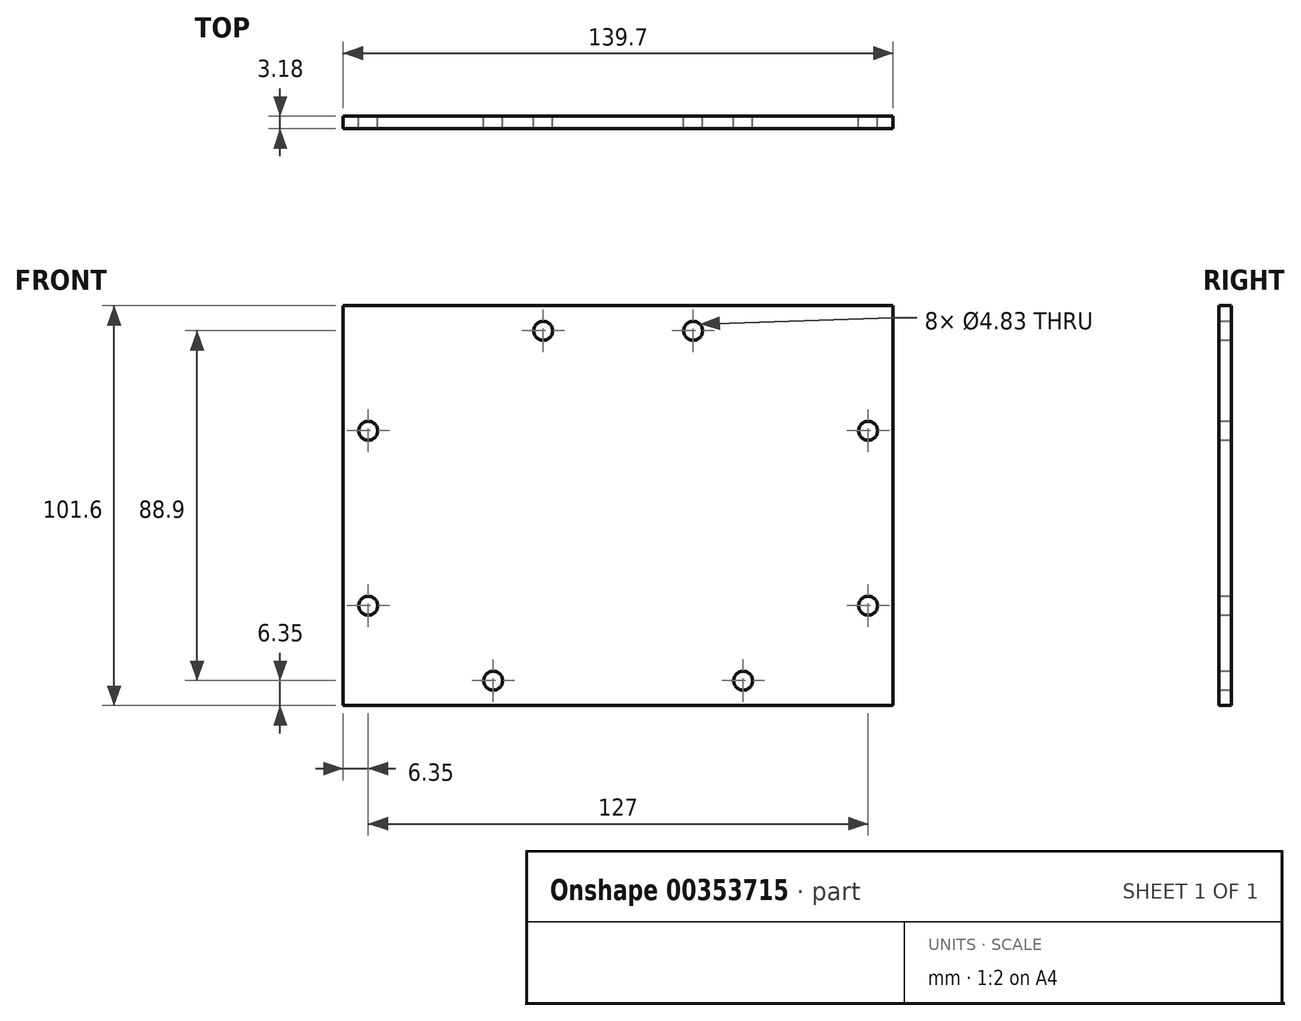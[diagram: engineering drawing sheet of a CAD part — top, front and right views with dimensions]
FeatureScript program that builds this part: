
annotation { "Feature Type Name" : "Feature", "Feature Type Description" : "" }
export const myFeature = defineFeature(function(context is Context, id is Id, definition is map)
    precondition{}
    {
        {
            var Q0;
            Q0=qCreatedBy(makeId("Front.planeOp"),FACE);
            var sketch = newSketch(context, id + "F0", { "sketchPlane" : qUnion([Q0])});
            skLineSegment(sketch, "E0.bottom", {"start": v(-69.85, 50.8) * mm, "end": v(69.85, 50.8) * mm});
            skLineSegment(sketch, "E0.top", {"start": v(-69.85, -50.8) * mm, "end": v(69.85, -50.8) * mm});
            skLineSegment(sketch, "E0.left", {"start": v(-69.85, 50.8) * mm, "end": v(-69.85, -50.8) * mm});
            skLineSegment(sketch, "E0.right", {"start": v(69.85, 50.8) * mm, "end": v(69.85, -50.8) * mm});
            skPoint(sketch, "E0.middle", {"position": v(0, 0) * mm});
            skSolve(sketch);
        }
        {
            var Q0;
            Q0 = qSketchRegion(id + "F0", true);
            extrude(context, id + "F1", {"entities" : qUnion([Q0]), "depth" : 3.17 * mm, "symmetric" : true});
        }
        {
            var Q0;
            Q0=makeQuery(id+"F1.opExtrude","CAP_FACE",FACE,{"disambiguationData":[OSD([sQuery(id+"F0.wireOp",EDGE,"E0.bottom"),sQuery(id+"F0.wireOp",EDGE,"E0.top"),sQuery(id+"F0.wireOp",EDGE,"E0.left"),sQuery(id+"F0.wireOp",EDGE,"E0.right")])],"isStart":false});
            var sketch = newSketch(context, id + "F2", { "sketchPlane" : qUnion([Q0])});
            skLineSegment(sketch, "E1", {"start": v(-69.85, 50.8) * mm, "end": v(-69.85, 0) * mm, "construction": true});
            skLineSegment(sketch, "E2", {"start": v(-69.85, 0) * mm, "end": v(-69.85, -25.4) * mm, "construction": true});
            skLineSegment(sketch, "E3", {"start": v(-69.85, 50.8) * mm, "end": v(-63.5, 50.8) * mm, "construction": true});
            skLineSegment(sketch, "E4", {"start": v(-63.5, 50.8) * mm, "end": v(-63.5, -50.8) * mm, "construction": true});
            skLineSegment(sketch, "E5", {"start": v(-69.85, 50.8) * mm, "end": v(-69.85, 19.05) * mm, "construction": true});
            skLineSegment(sketch, "E6", {"start": v(-69.85, 19.05) * mm, "end": v(69.85, 19.05) * mm, "construction": true});
            skPoint(sketch, "E7", {"position": v(-63.5, 19.05) * mm});
            skCircle(sketch, "E8", {"center": v(-63.5, 19.05) * mm, "radius": 2.41 * mm});
            skLineSegment(sketch, "E9", {"start": v(-69.85, -25.4) * mm, "end": v(69.85, -25.4) * mm, "construction": true});
            skPoint(sketch, "E10", {"position": v(-63.5, -25.4) * mm});
            skCircle(sketch, "E11", {"center": v(-63.5, -25.4) * mm, "radius": 2.41 * mm});
            skLineSegment(sketch, "E12", {"start": v(69.85, 50.8) * mm, "end": v(69.85, 44.45) * mm, "construction": true});
            skLineSegment(sketch, "E13", {"start": v(69.85, 44.45) * mm, "end": v(-69.85, 44.45) * mm, "construction": true});
            skLineSegment(sketch, "E14", {"start": v(69.85, 50.8) * mm, "end": v(63.5, 50.8) * mm, "construction": true});
            skLineSegment(sketch, "E15", {"start": v(63.5, 50.8) * mm, "end": v(63.5, -50.8) * mm, "construction": true});
            skLineSegment(sketch, "E16", {"start": v(69.85, -50.8) * mm, "end": v(69.85, -44.45) * mm, "construction": true});
            skLineSegment(sketch, "E17", {"start": v(69.85, -44.45) * mm, "end": v(-69.85, -44.45) * mm, "construction": true});
            skLineSegment(sketch, "E18", {"start": v(69.85, -50.8) * mm, "end": v(31.75, -50.8) * mm, "construction": true});
            skLineSegment(sketch, "E19", {"start": v(-69.85, -50.8) * mm, "end": v(-31.75, -50.8) * mm, "construction": true});
            skLineSegment(sketch, "E20", {"start": v(-31.75, -50.8) * mm, "end": v(-31.75, -44.45) * mm, "construction": true});
            skLineSegment(sketch, "E21", {"start": v(31.75, -50.8) * mm, "end": v(31.75, -44.45) * mm, "construction": true});
            skLineSegment(sketch, "E22", {"start": v(-69.85, 50.8) * mm, "end": v(-19.05, 50.8) * mm, "construction": true});
            skLineSegment(sketch, "E23", {"start": v(-69.85, 50.8) * mm, "end": v(19.05, 50.8) * mm, "construction": true});
            skLineSegment(sketch, "E24", {"start": v(-19.05, 50.8) * mm, "end": v(-19.05, 44.45) * mm, "construction": true});
            skLineSegment(sketch, "E25", {"start": v(19.05, 50.8) * mm, "end": v(19.05, 44.45) * mm, "construction": true});
            skCircle(sketch, "E26", {"center": v(-31.75, -44.45) * mm, "radius": 2.41 * mm});
            skCircle(sketch, "E27", {"center": v(31.75, -44.45) * mm, "radius": 2.41 * mm});
            skCircle(sketch, "E28", {"center": v(63.5, -25.4) * mm, "radius": 2.41 * mm});
            skCircle(sketch, "E29", {"center": v(63.5, 19.05) * mm, "radius": 2.41 * mm});
            skCircle(sketch, "E30", {"center": v(19.05, 44.45) * mm, "radius": 2.41 * mm});
            skCircle(sketch, "E31", {"center": v(-19.05, 44.45) * mm, "radius": 2.41 * mm});
            skSolve(sketch);
        }
        {
            var Q0;
            Q0 = qSketchRegion(id + "F2", true);
            extrude(context, id + "F3", {"entities" : qUnion([Q0]), "operationType" : NewBodyOperationType.REMOVE, "depth" : 25.4 * mm, "symmetric" : true});
        }
    });
